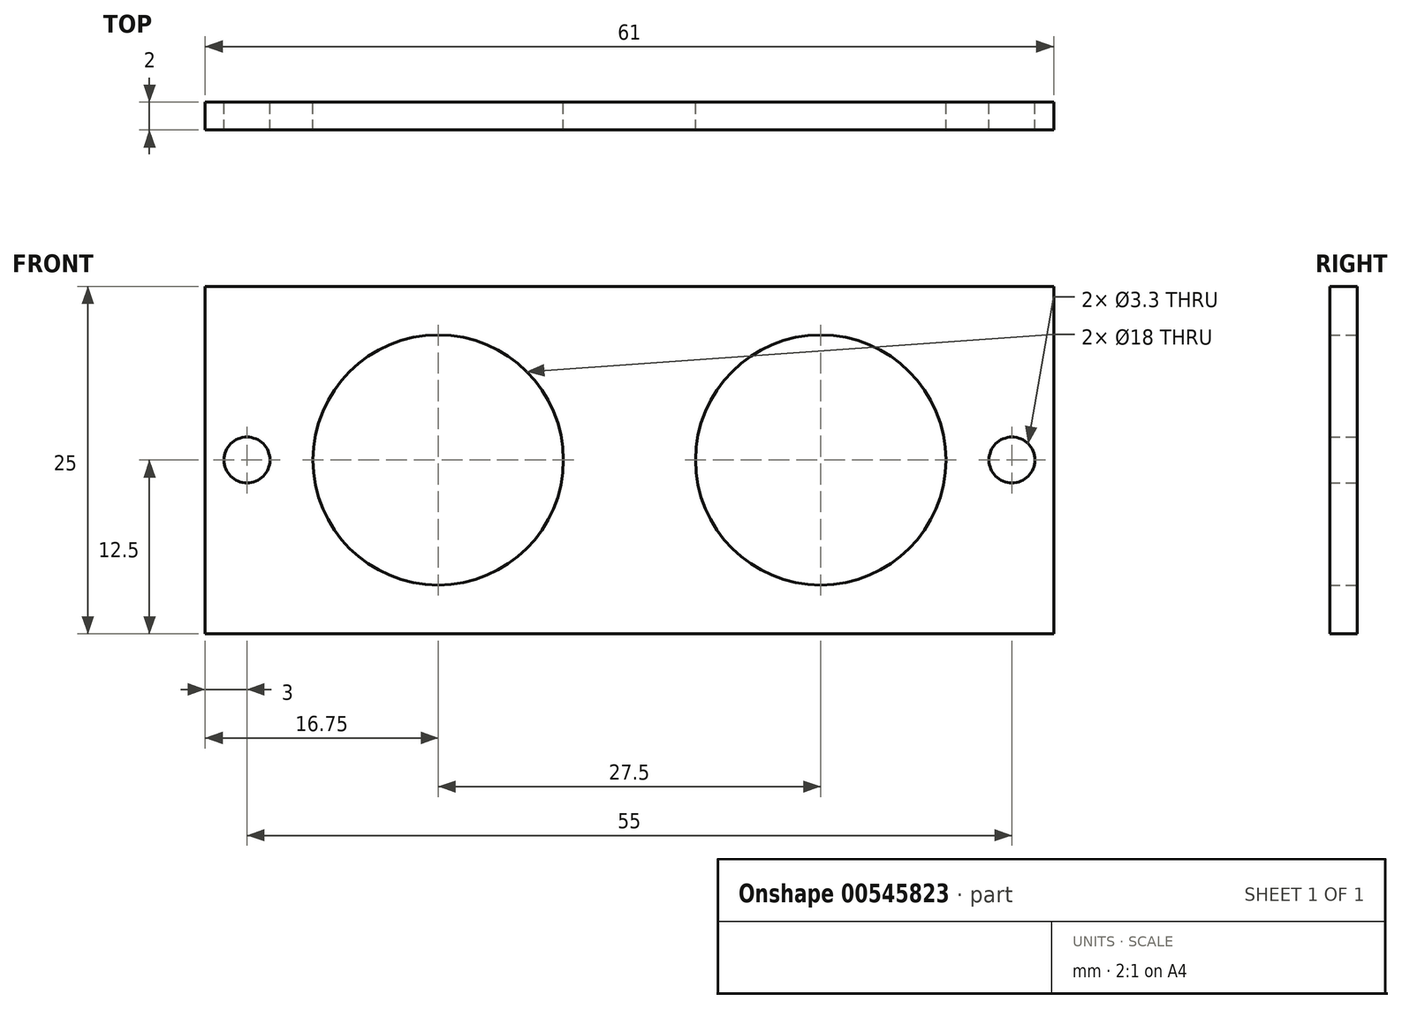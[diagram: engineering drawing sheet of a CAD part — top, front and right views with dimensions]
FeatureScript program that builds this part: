
annotation { "Feature Type Name" : "Feature", "Feature Type Description" : "" }
export const myFeature = defineFeature(function(context is Context, id is Id, definition is map)
    precondition{}
    {
        {
            var Q0;
            Q0=qCreatedBy(makeId("Front.planeOp"),FACE);
            var sketch = newSketch(context, id + "F0", { "sketchPlane" : qUnion([Q0])});
            skLineSegment(sketch, "E0.bottom", {"start": v(30.5, -12.5) * mm, "end": v(-30.5, -12.5) * mm});
            skLineSegment(sketch, "E0.top", {"start": v(30.5, 12.5) * mm, "end": v(-30.5, 12.5) * mm});
            skLineSegment(sketch, "E0.left", {"start": v(30.5, -12.5) * mm, "end": v(30.5, 12.5) * mm});
            skLineSegment(sketch, "E0.right", {"start": v(-30.5, -12.5) * mm, "end": v(-30.5, 12.5) * mm});
            skPoint(sketch, "E0.middle", {"position": v(0, 0) * mm});
            skCircle(sketch, "E1", {"center": v(-27.5, 0) * mm, "radius": 1.65 * mm});
            skCircle(sketch, "E2", {"center": v(27.5, 0) * mm, "radius": 1.65 * mm});
            skCircle(sketch, "E3", {"center": v(-13.75, 0) * mm, "radius": 9 * mm});
            skCircle(sketch, "E4", {"center": v(13.75, 0) * mm, "radius": 9 * mm});
            skSolve(sketch);
        }
        {
            var Q0;
            Q0=makeQuery(id+"F0.imprint","IMPRINT",FACE,{"disambiguationData":[TD([[makeQuery(id+"F0.imprint","IMPRINT",EDGE,{"derivedFrom":sQuery(id+"F0.wireOp",EDGE,"E0.bottom")}),-1.0]])]});
            extrude(context, id + "F1", {"entities" : qUnion([Q0]), "depth" : 2 * mm, "offsetDistance" : 25 * mm});
        }
    });
